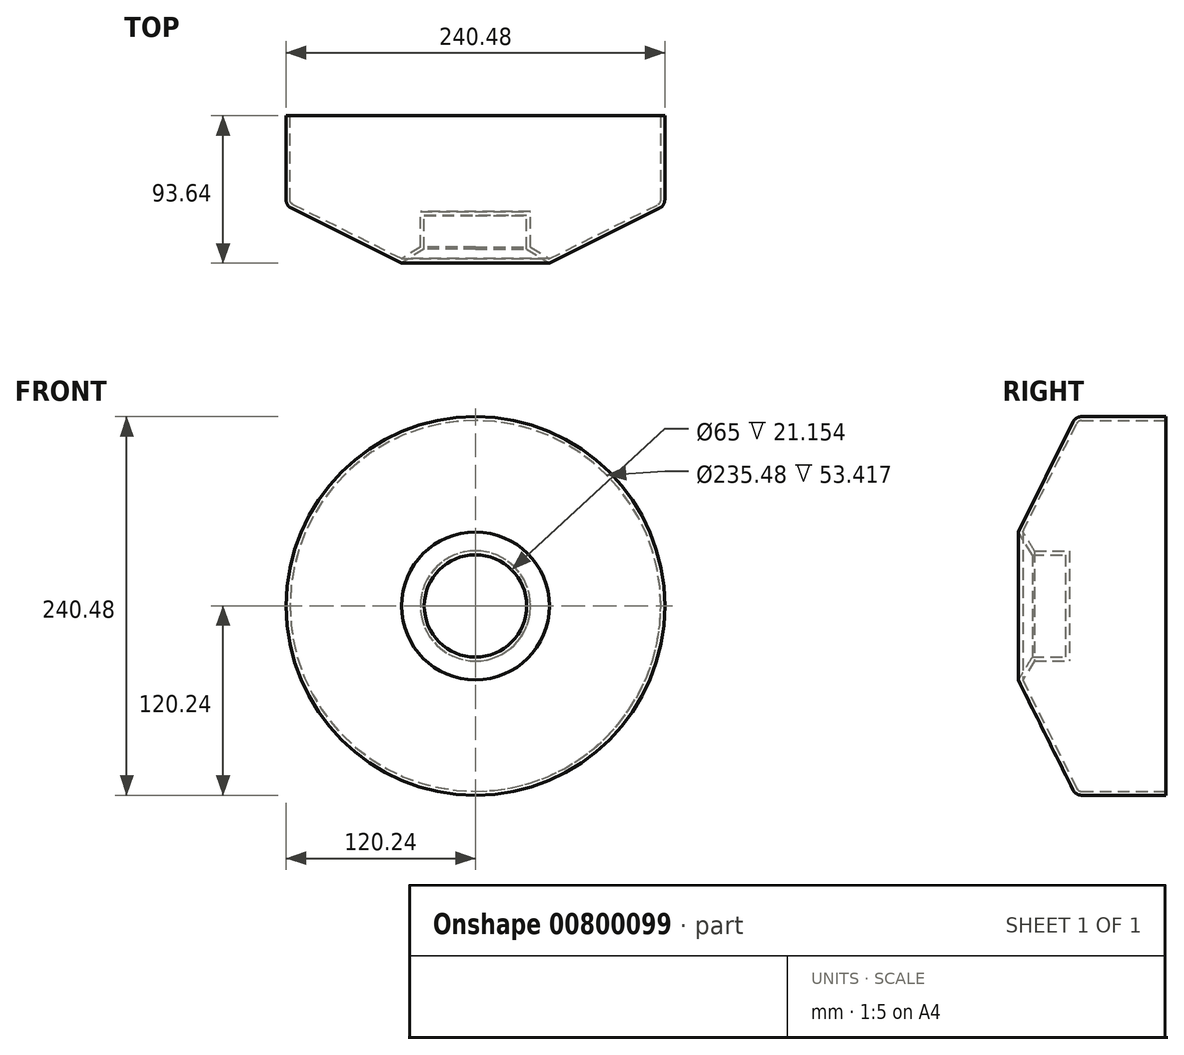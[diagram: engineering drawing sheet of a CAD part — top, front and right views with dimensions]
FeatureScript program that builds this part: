
annotation { "Feature Type Name" : "Feature", "Feature Type Description" : "" }
export const myFeature = defineFeature(function(context is Context, id is Id, definition is map)
    precondition{}
    {
        {
            var Q0;
            Q0=qCreatedBy(makeId("Top.planeOp"),FACE);
            var sketch = newSketch(context, id + "F0", { "sketchPlane" : qUnion([Q0])});
            skLineSegment(sketch, "E0", {"start": v(-120.24, 6.41) * mm, "end": v(-120.24, 63.54) * mm});
            skLineSegment(sketch, "E1", {"start": v(-120.24, 63.54) * mm, "end": v(0, 63.54) * mm});
            skLineSegment(sketch, "E2", {"start": v(0, 63.54) * mm, "end": v(0, 0) * mm});
            skLineSegment(sketch, "E3", {"start": v(0, 0) * mm, "end": v(-32.5, 0) * mm});
            skLineSegment(sketch, "E4", {"start": v(-32.5, 0) * mm, "end": v(-32.5, -37.31) * mm});
            skLineSegment(sketch, "E5", {"start": v(-32.5, -37.31) * mm, "end": v(-120.24, 6.41) * mm});
            skLineSegment(sketch, "E6", {"start": v(0, 91.53) * mm, "end": v(0, -53.63) * mm, "construction": true});
            skSolve(sketch);
        }
        {
            var Q0;
            Q0=makeQuery(id+"F0.imprint","IMPRINT",FACE,{"disambiguationData":[TD([[makeQuery(id+"F0.imprint","IMPRINT",EDGE,{"derivedFrom":sQuery(id+"F0.wireOp",EDGE,"E0")}),-1.0]])]});
            var Q1;
            Q1=sQuery(id+"F0.wireOp",EDGE,"E1");
            var Q2;
            Q2=sQuery(id+"F0.wireOp",EDGE,"E0");
            var Q3;
            Q3=sQuery(id+"F0.wireOp",EDGE,"E5");
            var Q4;
            Q4=sQuery(id+"F0.wireOp",EDGE,"E4");
            var Q5;
            Q5=sQuery(id+"F0.wireOp",EDGE,"E3");
            var Q6;
            Q6=sQuery(id+"F0.wireOp",EDGE,"E2");
            var Q7;
            Q7=sQuery(id+"F0.wireOp",EDGE,"E6");
            revolve(context, id + "F1", {"surfaceOperationType" : NewSurfaceOperationType.NEW, "entities" : qUnion([Q0]), "surfaceEntities" : qUnion([Q1, Q2, Q3, Q4, Q5, Q6]), "axis" : qUnion([Q7]), "revolveType" : RevolveType.FULL});
        }
        {
            var Q0;
            Q0=makeQuery(id+"F1.opRevolve","SWEPT_EDGE",EDGE,{"disambiguationData":[OSD([sQuery(id+"F0.wireOp",EDGE,"E0"),sQuery(id+"F0.wireOp",EDGE,"E5")])]});
            fillet(context, id + "F2", {"entities" : qUnion([Q0]), "radius" : 6 * mm, "tangentPropagation" : true, "allowEdgeOverflow" : false});
        }
        {
            var Q0;
            Q0=makeQuery(id+"F1.opRevolve","SWEPT_EDGE",EDGE,{"disambiguationData":[OSD([sQuery(id+"F0.wireOp",EDGE,"E4"),sQuery(id+"F0.wireOp",EDGE,"E5")])]});
            chamfer(context, id + "F3", {"entities" : qUnion([Q0]), "width" : 10 * mm, "tangentPropagation" : true});
        }
        {
            var Q0;
            Q0=makeQuery(id+"F1.opRevolve","SWEPT_FACE",FACE,{"disambiguationData":[OSD([sQuery(id+"F0.wireOp",EDGE,"E1")])]});
            var Q1;
            Q1=makeQuery(id+"F1.opRevolve","SWEPT_BODY",BODY,{"disambiguationData":[OSD([sQuery(id+"F0.wireOp",EDGE,"E0"),sQuery(id+"F0.wireOp",EDGE,"E1"),sQuery(id+"F0.wireOp",EDGE,"E2"),sQuery(id+"F0.wireOp",EDGE,"E3"),sQuery(id+"F0.wireOp",EDGE,"E4"),sQuery(id+"F0.wireOp",EDGE,"E5")])]});
            shell(context, id + "F4", {"entities" : qUnion([Q0]), "parts" : qUnion([Q1]), "thickness" : 2.5 * mm});
        }
    });
